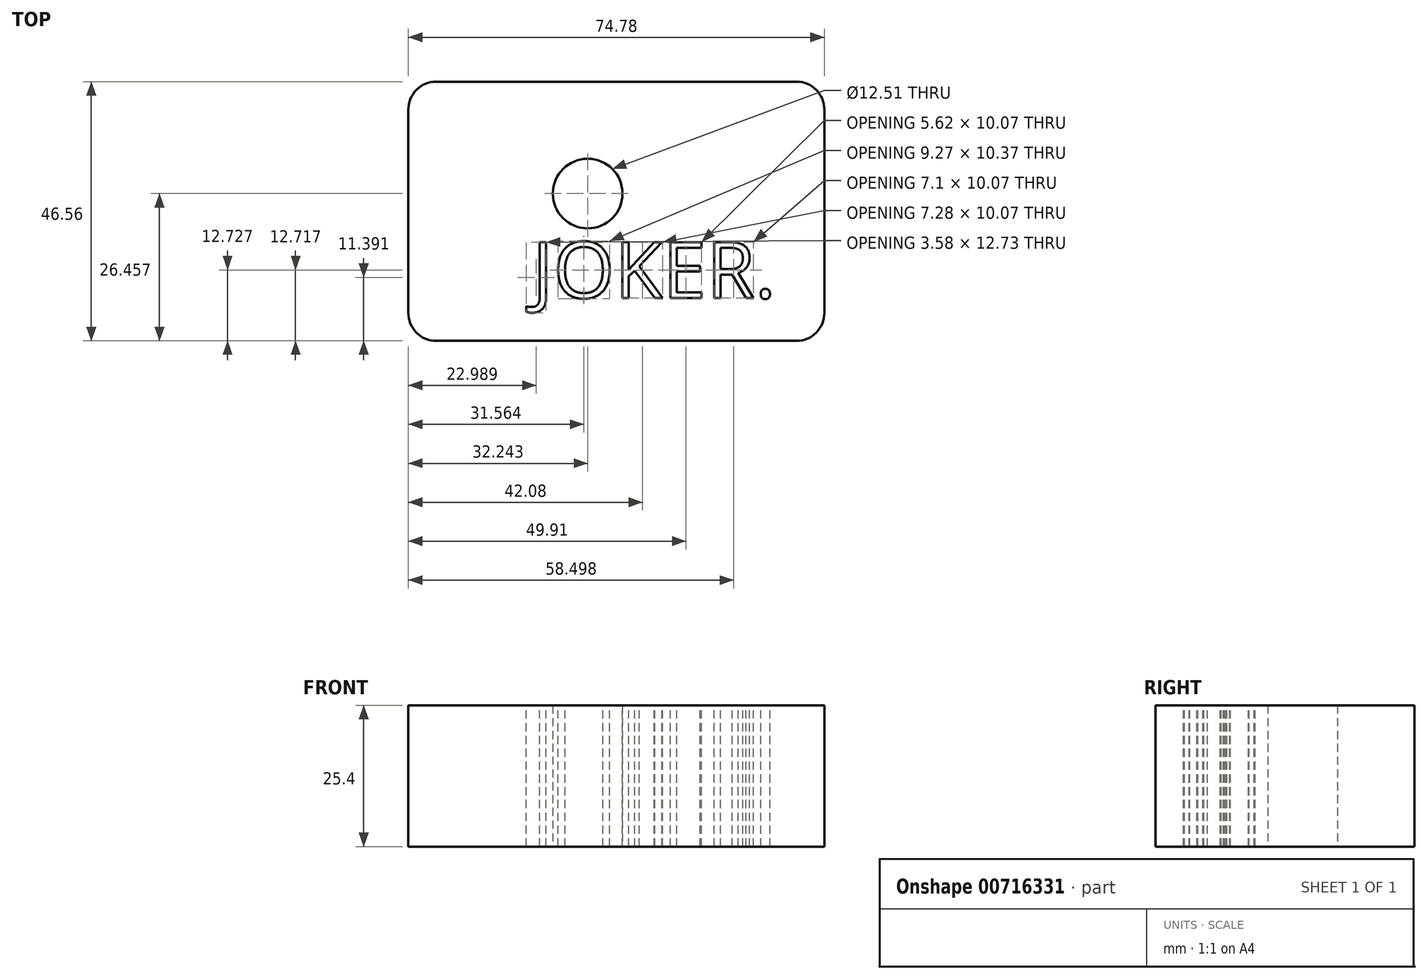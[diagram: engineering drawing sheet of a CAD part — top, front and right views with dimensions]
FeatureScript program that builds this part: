
annotation { "Feature Type Name" : "Feature", "Feature Type Description" : "" }
export const myFeature = defineFeature(function(context is Context, id is Id, definition is map)
    precondition{}
    {
        {
            var Q0;
            Q0=qCreatedBy(makeId("Top.planeOp"),FACE);
            var sketch = newSketch(context, id + "F0", { "sketchPlane" : qUnion([Q0])});
            skLineSegment(sketch, "E0.bottom", {"start": v(5, 0) * mm, "end": v(69.78, 0) * mm});
            skLineSegment(sketch, "E0.top", {"start": v(5, 46.56) * mm, "end": v(69.78, 46.56) * mm});
            skLineSegment(sketch, "E0.left", {"start": v(0, 5) * mm, "end": v(0, 41.56) * mm});
            skLineSegment(sketch, "E0.right", {"start": v(74.78, 5) * mm, "end": v(74.78, 41.56) * mm});
            skPoint(sketch, "E1.visualSharp", {"position": v(0, 0) * mm});
            skArc(sketch, "E1.filletArc", {"start": v(0, 5) * mm, "mid": v(1.46, 1.46) * mm, "end": v(5, 0) * mm});
            skPoint(sketch, "E2.visualSharp", {"position": v(74.78, 46.56) * mm});
            skArc(sketch, "E2.filletArc", {"start": v(74.78, 41.56) * mm, "mid": v(73.31, 45.1) * mm, "end": v(69.78, 46.56) * mm});
            skPoint(sketch, "E3.visualSharp", {"position": v(74.78, 0) * mm});
            skArc(sketch, "E3.filletArc", {"start": v(69.78, 0) * mm, "mid": v(73.31, 1.46) * mm, "end": v(74.78, 5) * mm});
            skPoint(sketch, "E4.visualSharp", {"position": v(0, 46.56) * mm});
            skArc(sketch, "E4.filletArc", {"start": v(5, 46.56) * mm, "mid": v(1.46, 45.1) * mm, "end": v(0, 41.56) * mm});
            skCircle(sketch, "E5", {"center": v(32.24, 26.46) * mm, "radius": 6.26 * mm});
            skSolve(sketch);
        }
        {
            var Q0;
            Q0 = qSketchRegion(id + "F0", true);
            extrude(context, id + "F1", {"entities" : qUnion([Q0]), "depth" : 25.4 * mm, "offsetDistance" : 25.4 * mm});
        }
        {
            var Q0;
            Q0=makeQuery(id+"F1.opExtrude","CAP_FACE",FACE,{"disambiguationData":[OSD([sQuery(id+"F0.wireOp",EDGE,"E0.bottom"),sQuery(id+"F0.wireOp",EDGE,"E0.top"),sQuery(id+"F0.wireOp",EDGE,"E0.left"),sQuery(id+"F0.wireOp",EDGE,"E0.right"),sQuery(id+"F0.wireOp",EDGE,"E1.filletArc"),sQuery(id+"F0.wireOp",EDGE,"E2.filletArc"),sQuery(id+"F0.wireOp",EDGE,"E3.filletArc"),sQuery(id+"F0.wireOp",EDGE,"E4.filletArc"),sQuery(id+"F0.wireOp",EDGE,"E5")])],"isStart":false});
            var sketch = newSketch(context, id + "F2", { "sketchPlane" : qUnion([Q0])});
            skSolve(sketch);
        }
        {
            var Q0;
            Q0=makeQuery(id+"F2.imprint","IMPRINT",FACE,{"disambiguationData":[TD([[makeQuery(id+"F2.imprint","IMPRINT",EDGE,{"derivedFrom":makeQuery(id+"F1.opExtrude","CAP_EDGE",EDGE,{"disambiguationData":[OSD([sQuery(id+"F0.wireOp",EDGE,"E0.bottom")])],"isStart":false})}),1.0]])]});
            var sketch = newSketch(context, id + "F3", { "sketchPlane" : qUnion([Q0])});
            skSolve(sketch);
        }
        {
            var Q0;
            Q0=makeQuery(id+"F3.imprint","IMPRINT",FACE,{"disambiguationData":[TD([[makeQuery(id+"F3.imprint","IMPRINT",EDGE,{"derivedFrom":makeQuery(id+"F2.imprint","IMPRINT",EDGE,{"derivedFrom":makeQuery(id+"F1.opExtrude","CAP_EDGE",EDGE,{"disambiguationData":[OSD([sQuery(id+"F0.wireOp",EDGE,"E0.bottom")])],"isStart":false})})}),1.0]])]});
            var sketch = newSketch(context, id + "F4", { "sketchPlane" : qUnion([Q0])});
            skText(sketch, "E6", { "text": "JOKER.", "fontName": "OpenSans-Regular.ttf"});
            const initialGuessF4  = {"E6": [0.0223, 0.00768, 1, 0, 0.01016]};
            skSetInitialGuess(sketch, initialGuessF4);
            skSolve(sketch);
        }
        {
            var Q0;
            Q0=makeQuery(id+"F4.imprint","IMPRINT",FACE,{"disambiguationData":[TD([[makeQuery(id+"F4.imprint","IMPRINT",EDGE,{"derivedFrom":sQuery(id+"F4.wireOp",EDGE,"E6.sketch_text.stroke-10")}),-1.0]])]});
            var Q1;
            Q1=makeQuery(id+"F4.imprint","IMPRINT",FACE,{"disambiguationData":[TD([[makeQuery(id+"F4.imprint","IMPRINT",EDGE,{"derivedFrom":sQuery(id+"F4.wireOp",EDGE,"E6.sketch_text.stroke-38")}),-1.0]])]});
            var Q2;
            Q2=makeQuery(id+"F4.imprint","IMPRINT",FACE,{"disambiguationData":[TD([[makeQuery(id+"F4.imprint","IMPRINT",EDGE,{"derivedFrom":sQuery(id+"F4.wireOp",EDGE,"E6.sketch_text.stroke-50")}),-1.0]])]});
            var Q3;
            Q3=makeQuery(id+"F4.imprint","IMPRINT",FACE,{"disambiguationData":[TD([[makeQuery(id+"F4.imprint","IMPRINT",EDGE,{"derivedFrom":sQuery(id+"F4.wireOp",EDGE,"E6.sketch_text.stroke-26")}),-1.0]])]});
            var Q4;
            Q4=makeQuery(id+"F4.imprint","IMPRINT",FACE,{"disambiguationData":[TD([[makeQuery(id+"F4.imprint","IMPRINT",EDGE,{"derivedFrom":sQuery(id+"F4.wireOp",EDGE,"E6.sketch_text.stroke-0")}),-1.0]])]});
            var Q5;
            Q5=makeQuery(id+"F4.imprint","IMPRINT",FACE,{"disambiguationData":[TD([[makeQuery(id+"F4.imprint","IMPRINT",EDGE,{"derivedFrom":sQuery(id+"F4.wireOp",EDGE,"E6.sketch_text.stroke-68")}),-1.0]])]});
            extrude(context, id + "F5", {"entities" : qUnion([Q0, Q1, Q2, Q3, Q4, Q5]), "operationType" : NewBodyOperationType.REMOVE, "endBound" : BoundingType.THROUGH_ALL, "oppositeDirection" : true, "depth" : 25.4 * mm, "offsetDistance" : 25.4 * mm});
        }
    });
